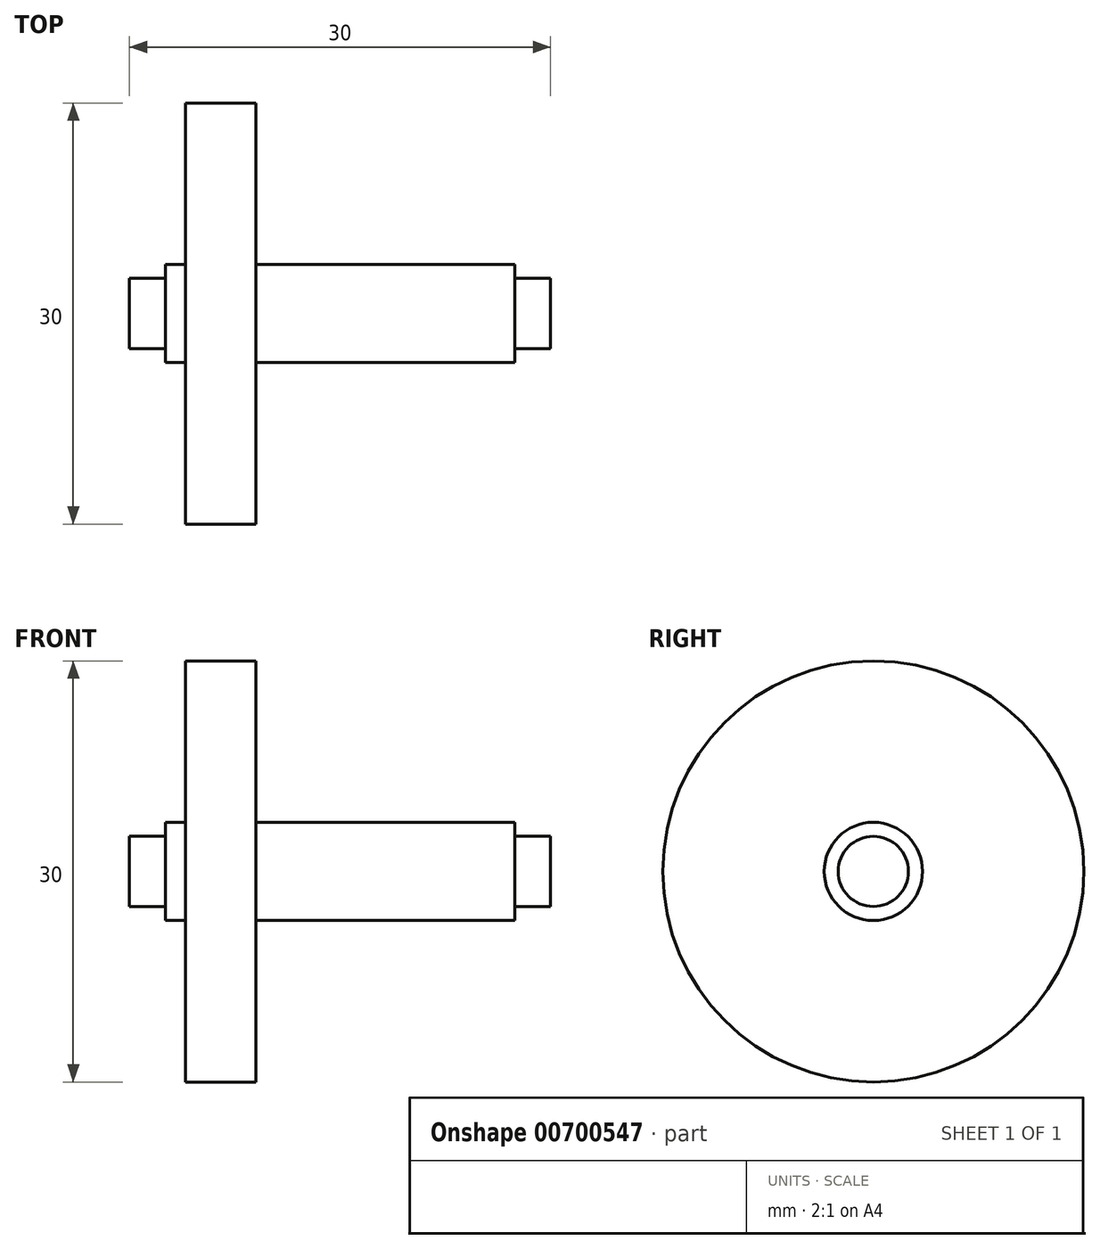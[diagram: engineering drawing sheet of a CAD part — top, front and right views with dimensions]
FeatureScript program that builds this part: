
annotation { "Feature Type Name" : "Feature", "Feature Type Description" : "" }
export const myFeature = defineFeature(function(context is Context, id is Id, definition is map)
    precondition{}
    {
        {
            var Q0;
            Q0=qCreatedBy(makeId("Top.planeOp"),FACE);
            var sketch = newSketch(context, id + "F0", { "sketchPlane" : qUnion([Q0])});
            skLineSegment(sketch, "E0.bottom", {"start": v(12.45, -3.5) * mm, "end": v(-12.45, -3.5) * mm});
            skLineSegment(sketch, "E0.top", {"start": v(12.45, 3.5) * mm, "end": v(-12.45, 3.5) * mm});
            skLineSegment(sketch, "E0.left", {"start": v(12.45, -3.5) * mm, "end": v(12.45, 3.5) * mm});
            skLineSegment(sketch, "E0.right", {"start": v(-12.45, -3.5) * mm, "end": v(-12.45, 3.5) * mm});
            skPoint(sketch, "E0.middle", {"position": v(0, 0) * mm});
            skLineSegment(sketch, "E1.bottom", {"start": v(-6, -15) * mm, "end": v(-11, -15) * mm});
            skLineSegment(sketch, "E1.top", {"start": v(-6, 15) * mm, "end": v(-11, 15) * mm});
            skLineSegment(sketch, "E1.left", {"start": v(-6, -15) * mm, "end": v(-6, 15) * mm});
            skLineSegment(sketch, "E1.right", {"start": v(-11, -15) * mm, "end": v(-11, 15) * mm});
            skPoint(sketch, "E1.middle", {"position": v(-8.5, 0) * mm});
            skLineSegment(sketch, "E2", {"start": v(-53.7, 0) * mm, "end": v(15.45, 0) * mm, "construction": true});
            skLineSegment(sketch, "E3.bottom", {"start": v(15, -2.5) * mm, "end": v(-15, -2.5) * mm});
            skLineSegment(sketch, "E3.top", {"start": v(15, 2.5) * mm, "end": v(-15, 2.5) * mm});
            skLineSegment(sketch, "E3.left", {"start": v(15, -2.5) * mm, "end": v(15, 2.5) * mm});
            skLineSegment(sketch, "E3.right", {"start": v(-15, -2.5) * mm, "end": v(-15, 2.5) * mm});
            skLineSegment(sketch, "E4", {"start": v(-15, 0) * mm, "end": v(15, 0) * mm});
            skSolve(sketch);
        }
        {
            var Q0;
            {var subQ5=sQuery(id+"F0.wireOp",EDGE,"E1.top");Q0=makeQuery(id+"F0.imprint","IMPRINT",FACE,{"disambiguationData":[TD([[makeQuery(id+"F0.imprint","IMPRINT",EDGE,{"derivedFrom":subQ5}),1.0]])]});}
            var Q1;
            {var subQ0=sQuery(id+"F0.wireOp",EDGE,"E0.right");var subQ1=sQuery(id+"F0.wireOp",EDGE,"E0.top");var subQ2=makeQuery(id+"F0.imprint","INTERSECT",VERTEX,{"derivedFrom":[subQ1,subQ0]});Q1=makeQuery(id+"F0.imprint","IMPRINT",FACE,{"disambiguationData":[TD([[makeQuery(id+"F0.imprint","IMPRINT",EDGE,{"disambiguationData":[TD([[subQ2,1.0]])],"derivedFrom":subQ1}),1.0]])]});}
            var Q2;
            {var subQ0=sQuery(id+"F0.wireOp",EDGE,"E3.top");var subQ1=sQuery(id+"F0.wireOp",EDGE,"E0.right");var subQ2=makeQuery(id+"F0.imprint","INTERSECT",VERTEX,{"derivedFrom":[subQ1,subQ0]});Q2=makeQuery(id+"F0.imprint","IMPRINT",FACE,{"disambiguationData":[TD([[makeQuery(id+"F0.imprint","IMPRINT",EDGE,{"disambiguationData":[TD([[subQ2,1.0]])],"derivedFrom":subQ1}),-1.0]])]});}
            var Q3;
            {var subQ0=sQuery(id+"F0.wireOp",EDGE,"E3.top");var subQ1=sQuery(id+"F0.wireOp",EDGE,"E0.right");var subQ2=makeQuery(id+"F0.imprint","INTERSECT",VERTEX,{"derivedFrom":[subQ1,subQ0]});Q3=makeQuery(id+"F0.imprint","IMPRINT",FACE,{"disambiguationData":[TD([[makeQuery(id+"F0.imprint","IMPRINT",EDGE,{"disambiguationData":[TD([[subQ2,1.0]])],"derivedFrom":subQ1}),1.0]])]});}
            var Q4;
            {var subQ0=sQuery(id+"F0.wireOp",EDGE,"E4");var subQ1=sQuery(id+"F0.wireOp",EDGE,"E1.left");var subQ2=makeQuery(id+"F0.imprint","INTERSECT",VERTEX,{"derivedFrom":[subQ1,subQ0]});Q4=makeQuery(id+"F0.imprint","IMPRINT",FACE,{"disambiguationData":[TD([[makeQuery(id+"F0.imprint","IMPRINT",EDGE,{"disambiguationData":[TD([[subQ2,-1.0]])],"derivedFrom":subQ1}),1.0]])]});}
            var Q5;
            {var subQ0=sQuery(id+"F0.wireOp",EDGE,"E1.left");var subQ1=sQuery(id+"F0.wireOp",EDGE,"E0.top");var subQ2=makeQuery(id+"F0.imprint","INTERSECT",VERTEX,{"derivedFrom":[subQ1,subQ0]});Q5=makeQuery(id+"F0.imprint","IMPRINT",FACE,{"disambiguationData":[TD([[makeQuery(id+"F0.imprint","IMPRINT",EDGE,{"disambiguationData":[TD([[subQ2,-1.0]])],"derivedFrom":subQ1}),1.0]])]});}
            var Q6;
            {var subQ0=sQuery(id+"F0.wireOp",EDGE,"E0.left");var subQ1=sQuery(id+"F0.wireOp",EDGE,"E0.top");var subQ2=makeQuery(id+"F0.imprint","INTERSECT",VERTEX,{"derivedFrom":[subQ1,subQ0]});Q6=makeQuery(id+"F0.imprint","IMPRINT",FACE,{"disambiguationData":[TD([[makeQuery(id+"F0.imprint","IMPRINT",EDGE,{"disambiguationData":[TD([[subQ2,-1.0]])],"derivedFrom":subQ1}),1.0]])]});}
            var Q7;
            {var subQ0=sQuery(id+"F0.wireOp",EDGE,"E3.top");var subQ1=sQuery(id+"F0.wireOp",EDGE,"E0.left");var subQ2=makeQuery(id+"F0.imprint","INTERSECT",VERTEX,{"derivedFrom":[subQ1,subQ0]});Q7=makeQuery(id+"F0.imprint","IMPRINT",FACE,{"disambiguationData":[TD([[makeQuery(id+"F0.imprint","IMPRINT",EDGE,{"disambiguationData":[TD([[subQ2,1.0]])],"derivedFrom":subQ1}),1.0]])]});}
            var Q8;
            {var subQ0=sQuery(id+"F0.wireOp",EDGE,"E3.top");var subQ1=sQuery(id+"F0.wireOp",EDGE,"E0.left");var subQ2=makeQuery(id+"F0.imprint","INTERSECT",VERTEX,{"derivedFrom":[subQ1,subQ0]});Q8=makeQuery(id+"F0.imprint","IMPRINT",FACE,{"disambiguationData":[TD([[makeQuery(id+"F0.imprint","IMPRINT",EDGE,{"disambiguationData":[TD([[subQ2,1.0]])],"derivedFrom":subQ1}),-1.0]])]});}
            var Q9;
            Q9=sQuery(id+"F0.wireOp",EDGE,"E2");
            revolve(context, id + "F1", {"entities" : qUnion([Q0, Q1, Q2, Q3, Q4, Q5, Q6, Q7, Q8]), "axis" : qUnion([Q9]), "revolveType" : RevolveType.FULL});
        }
    });
